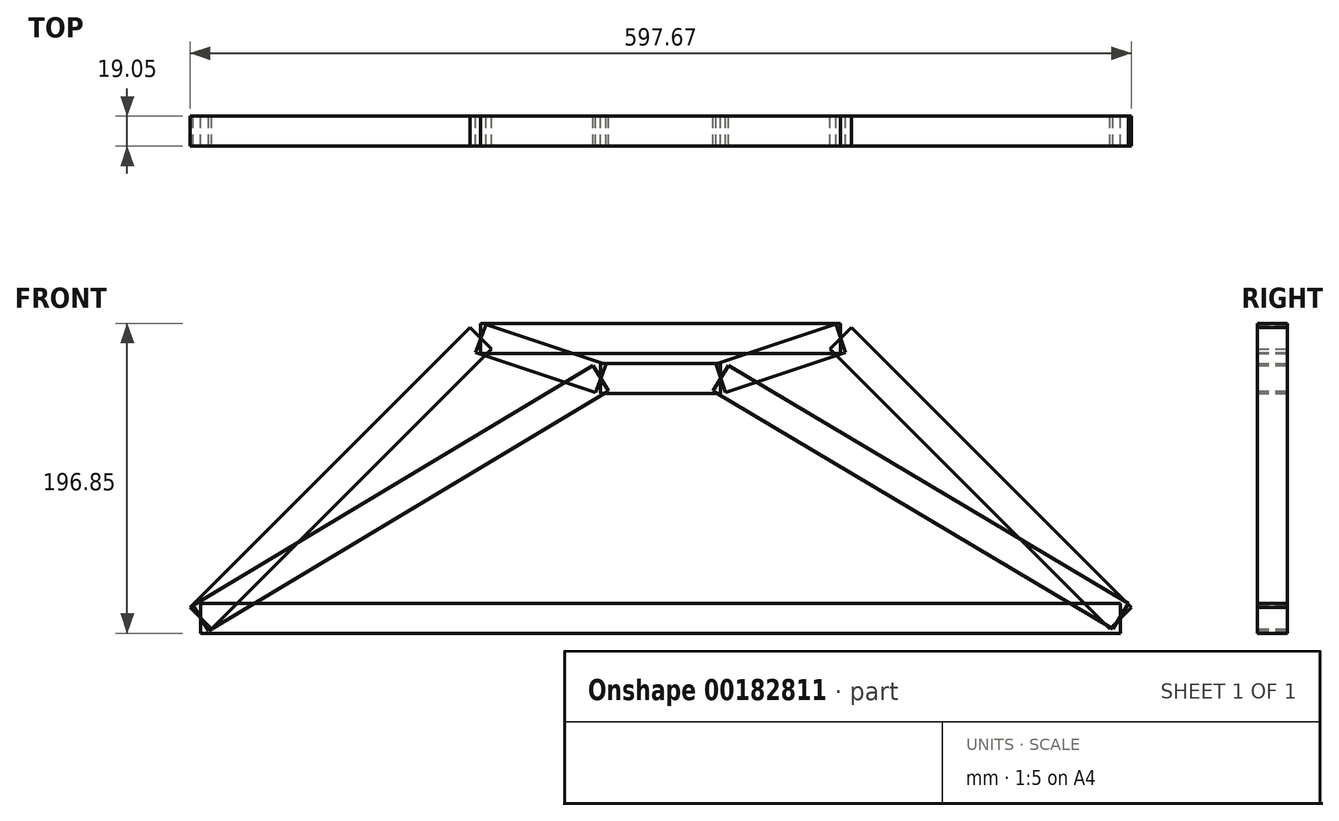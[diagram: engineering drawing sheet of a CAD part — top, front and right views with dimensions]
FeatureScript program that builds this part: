
annotation { "Feature Type Name" : "Feature", "Feature Type Description" : "" }
export const myFeature = defineFeature(function(context is Context, id is Id, definition is map)
    precondition{}
    {
        {
            var Q0;
            Q0=qCreatedBy(makeId("Front.planeOp"),FACE);
            var sketch = newSketch(context, id + "F0", { "sketchPlane" : qUnion([Q0])});
            skLineSegment(sketch, "E0", {"start": v(-420.77, 0) * mm, "end": v(163.43, 0) * mm});
            skLineSegment(sketch, "E1", {"start": v(-420.77, 0) * mm, "end": v(-242.97, 177.8) * mm});
            skLineSegment(sketch, "E2", {"start": v(-242.97, 177.8) * mm, "end": v(-14.37, 177.8) * mm});
            skLineSegment(sketch, "E3", {"start": v(-14.37, 177.8) * mm, "end": v(163.43, 0) * mm});
            skPoint(sketch, "E4.endSnap0", {"position": v(-128.67, 0) * mm});
            skLineSegment(sketch, "E5", {"start": v(-128.67, 152.4) * mm, "end": v(-166.77, 152.4) * mm});
            skLineSegment(sketch, "E6", {"start": v(-166.77, 152.4) * mm, "end": v(-128.67, 152.4) * mm});
            skLineSegment(sketch, "E7", {"start": v(-90.57, 152.4) * mm, "end": v(-128.67, 152.4) * mm});
            skLineSegment(sketch, "E8", {"start": v(-166.77, 152.4) * mm, "end": v(-90.57, 152.4) * mm});
            skLineSegment(sketch, "E9", {"start": v(-90.57, 152.4) * mm, "end": v(-14.37, 177.8) * mm});
            skLineSegment(sketch, "E10", {"start": v(-166.77, 152.4) * mm, "end": v(-420.77, 0) * mm});
            skLineSegment(sketch, "E11", {"start": v(-242.97, 177.8) * mm, "end": v(-166.77, 152.4) * mm});
            skLineSegment(sketch, "E12", {"start": v(-90.57, 152.4) * mm, "end": v(163.43, 0) * mm});
            skSolve(sketch);
        }
        {
            var Q0;
            Q0=qCreatedBy(makeId("Front.planeOp"),FACE);
            var sketch = newSketch(context, id + "F1", { "sketchPlane" : qUnion([Q0])});
            skLineSegment(sketch, "E13", {"start": v(-427.5, 6.74) * mm, "end": v(-249.7, 184.54) * mm});
            skLineSegment(sketch, "E14", {"start": v(-249.7, 184.54) * mm, "end": v(-236.23, 171.06) * mm});
            skLineSegment(sketch, "E15", {"start": v(-236.23, 171.06) * mm, "end": v(-414.03, -6.74) * mm});
            skLineSegment(sketch, "E16", {"start": v(-414.03, -6.74) * mm, "end": v(-427.5, 6.74) * mm});
            skSolve(sketch);
        }
        {
            var Q0;
            Q0=qCreatedBy(makeId("Front.planeOp"),FACE);
            var sketch = newSketch(context, id + "F2", { "sketchPlane" : qUnion([Q0])});
            skLineSegment(sketch, "E17", {"start": v(-242.97, 187.32) * mm, "end": v(-242.97, 168.27) * mm});
            skLineSegment(sketch, "E18", {"start": v(-242.97, 168.27) * mm, "end": v(-14.37, 168.27) * mm});
            skLineSegment(sketch, "E19", {"start": v(-14.37, 168.27) * mm, "end": v(-14.37, 187.32) * mm});
            skLineSegment(sketch, "E20", {"start": v(-14.37, 187.32) * mm, "end": v(-242.97, 187.32) * mm});
            skSolve(sketch);
        }
        {
            var Q0;
            Q0=qCreatedBy(makeId("Front.planeOp"),FACE);
            var sketch = newSketch(context, id + "F3", { "sketchPlane" : qUnion([Q0])});
            skLineSegment(sketch, "E21", {"start": v(-246.3, 168.87) * mm, "end": v(-239.65, 186.73) * mm});
            skLineSegment(sketch, "E22", {"start": v(-239.65, 186.73) * mm, "end": v(-163.45, 161.33) * mm});
            skLineSegment(sketch, "E23", {"start": v(-170.09, 143.47) * mm, "end": v(-246.3, 168.87) * mm});
            skLineSegment(sketch, "E24", {"start": v(-170.09, 143.47) * mm, "end": v(-163.45, 161.33) * mm});
            skSolve(sketch);
        }
        {
            var Q0;
            Q0=qCreatedBy(makeId("Front.planeOp"),FACE);
            var sketch = newSketch(context, id + "F4", { "sketchPlane" : qUnion([Q0])});
            skLineSegment(sketch, "E25", {"start": v(-166.77, 142.87) * mm, "end": v(-90.57, 142.87) * mm});
            skLineSegment(sketch, "E26", {"start": v(-90.57, 142.87) * mm, "end": v(-90.57, 161.92) * mm});
            skLineSegment(sketch, "E27", {"start": v(-90.57, 161.92) * mm, "end": v(-166.77, 161.92) * mm});
            skLineSegment(sketch, "E28", {"start": v(-166.77, 161.92) * mm, "end": v(-166.77, 142.87) * mm});
            skSolve(sketch);
        }
        {
            var Q0;
            Q0=qCreatedBy(makeId("Front.planeOp"),FACE);
            var sketch = newSketch(context, id + "F5", { "sketchPlane" : qUnion([Q0])});
            skLineSegment(sketch, "E29", {"start": v(-87.56, 143.36) * mm, "end": v(-11.36, 168.76) * mm});
            skLineSegment(sketch, "E30", {"start": v(-11.36, 168.76) * mm, "end": v(-17.38, 186.84) * mm});
            skLineSegment(sketch, "E31", {"start": v(-17.38, 186.84) * mm, "end": v(-93.58, 161.44) * mm});
            skLineSegment(sketch, "E32", {"start": v(-93.58, 161.44) * mm, "end": v(-87.56, 143.36) * mm});
            skSolve(sketch);
        }
        {
            var Q0;
            Q0=qCreatedBy(makeId("Front.planeOp"),FACE);
            var sketch = newSketch(context, id + "F6", { "sketchPlane" : qUnion([Q0])});
            skLineSegment(sketch, "E33", {"start": v(-415.87, -8.17) * mm, "end": v(-161.87, 144.23) * mm});
            skLineSegment(sketch, "E34", {"start": v(-161.87, 144.23) * mm, "end": v(-171.67, 160.57) * mm});
            skLineSegment(sketch, "E35", {"start": v(-171.67, 160.57) * mm, "end": v(-425.67, 8.17) * mm});
            skLineSegment(sketch, "E36", {"start": v(-425.67, 8.17) * mm, "end": v(-415.87, -8.17) * mm});
            skSolve(sketch);
        }
        {
            var Q0;
            Q0=qCreatedBy(makeId("Front.planeOp"),FACE);
            var sketch = newSketch(context, id + "F7", { "sketchPlane" : qUnion([Q0])});
            skLineSegment(sketch, "E37", {"start": v(156.7, -6.74) * mm, "end": v(-21.1, 171.06) * mm});
            skLineSegment(sketch, "E38", {"start": v(-21.1, 171.06) * mm, "end": v(-7.63, 184.53) * mm});
            skLineSegment(sketch, "E39", {"start": v(-7.63, 184.53) * mm, "end": v(170.17, 6.74) * mm});
            skLineSegment(sketch, "E40", {"start": v(170.17, 6.74) * mm, "end": v(156.7, -6.74) * mm});
            skSolve(sketch);
        }
        {
            var Q0;
            Q0=qCreatedBy(makeId("Front.planeOp"),FACE);
            var sketch = newSketch(context, id + "F8", { "sketchPlane" : qUnion([Q0])});
            skLineSegment(sketch, "E41", {"start": v(-420.77, -9.53) * mm, "end": v(163.43, -9.53) * mm});
            skLineSegment(sketch, "E42", {"start": v(163.43, -9.53) * mm, "end": v(163.43, 9.52) * mm});
            skLineSegment(sketch, "E43", {"start": v(163.43, 9.52) * mm, "end": v(-420.77, 9.52) * mm});
            skLineSegment(sketch, "E44", {"start": v(-420.77, 9.52) * mm, "end": v(-420.77, -9.53) * mm});
            skSolve(sketch);
        }
        {
            var Q0;
            Q0=qCreatedBy(makeId("Front.planeOp"),FACE);
            var sketch = newSketch(context, id + "F9", { "sketchPlane" : qUnion([Q0])});
            skLineSegment(sketch, "E45", {"start": v(-95.43, 144.21) * mm, "end": v(-85.7, 160.59) * mm});
            skLineSegment(sketch, "E46", {"start": v(-85.7, 160.59) * mm, "end": v(168.3, 9.58) * mm});
            skLineSegment(sketch, "E47", {"start": v(168.3, 9.58) * mm, "end": v(158.57, -6.8) * mm});
            skLineSegment(sketch, "E48", {"start": v(158.57, -6.8) * mm, "end": v(-95.43, 144.21) * mm});
            skSolve(sketch);
        }
        {
            var Q0;
            Q0=makeQuery(id+"F5.imprint","IMPRINT",FACE,{"disambiguationData":[TD([[makeQuery(id+"F5.imprint","IMPRINT",EDGE,{"derivedFrom":sQuery(id+"F5.wireOp",EDGE,"E29")}),1.0]])]});
            var Q1;
            Q1=makeQuery(id+"F8.imprint","IMPRINT",FACE,{"disambiguationData":[TD([[makeQuery(id+"F8.imprint","IMPRINT",EDGE,{"derivedFrom":sQuery(id+"F8.wireOp",EDGE,"E41")}),1.0]])]});
            var Q2;
            Q2=makeQuery(id+"F6.imprint","IMPRINT",FACE,{"disambiguationData":[TD([[makeQuery(id+"F6.imprint","IMPRINT",EDGE,{"derivedFrom":sQuery(id+"F6.wireOp",EDGE,"E33")}),1.0]])]});
            var Q3;
            Q3=makeQuery(id+"F7.imprint","IMPRINT",FACE,{"disambiguationData":[TD([[makeQuery(id+"F7.imprint","IMPRINT",EDGE,{"derivedFrom":sQuery(id+"F7.wireOp",EDGE,"E37")}),-1.0]])]});
            var Q4;
            Q4=makeQuery(id+"F9.imprint","IMPRINT",FACE,{"disambiguationData":[TD([[makeQuery(id+"F9.imprint","IMPRINT",EDGE,{"derivedFrom":sQuery(id+"F9.wireOp",EDGE,"E45")}),-1.0]])]});
            var Q5;
            Q5=makeQuery(id+"F4.imprint","IMPRINT",FACE,{"disambiguationData":[TD([[makeQuery(id+"F4.imprint","IMPRINT",EDGE,{"derivedFrom":sQuery(id+"F4.wireOp",EDGE,"E25")}),1.0]])]});
            var Q6;
            Q6=makeQuery(id+"F1.imprint","IMPRINT",FACE,{"disambiguationData":[TD([[makeQuery(id+"F1.imprint","IMPRINT",EDGE,{"derivedFrom":sQuery(id+"F1.wireOp",EDGE,"E13")}),-1.0]])]});
            var Q7;
            Q7=makeQuery(id+"F2.imprint","IMPRINT",FACE,{"disambiguationData":[TD([[makeQuery(id+"F2.imprint","IMPRINT",EDGE,{"derivedFrom":sQuery(id+"F2.wireOp",EDGE,"E17")}),1.0]])]});
            var Q8;
            Q8=makeQuery(id+"F3.imprint","IMPRINT",FACE,{"disambiguationData":[TD([[makeQuery(id+"F3.imprint","IMPRINT",EDGE,{"derivedFrom":sQuery(id+"F3.wireOp",EDGE,"E21")}),-1.0]])]});
            extrude(context, id + "F10", {"entities" : qUnion([Q0, Q1, Q2, Q3, Q4, Q5, Q6, Q7, Q8]), "depth" : 19.05 * mm});
        }
    });
